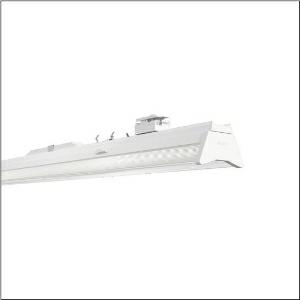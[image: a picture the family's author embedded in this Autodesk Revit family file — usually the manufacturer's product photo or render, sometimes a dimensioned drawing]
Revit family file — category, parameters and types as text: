
# Revit family: licross_r__11_performance_tw_51td16tnt85x_7c56
name_source: partatom
category: Lighting Fixtures
units: mm (PartAtom-declared; Revit-internal decimal feet)

## family parameters
Cut with Voids When Loaded = No
Host = Face
Light Source = No
Part Type = Normal
Room Calculation Point = No
Round Connector Dimension = Use Diameter
Shared = No

## types (1)
- --- (1 x LED 2700 K ... 6500 K, 8930 lm, 56 W, 2700K)
    Apparent Load = 56 VA
    CIE Flux Codes = 63 87 95 78 100
    Color Rendering = 80
    Color Temperature = 2700K
    Default Elevation = 1800 mm
    Description = Licross® 11 Performance TW, luminaire insert, of sheet steel, galvanised, coil coated, white, length: 1.500mm, width: 120mm, height: 123mm, LED rated luminous flux: 8.930lm, light colour: 8tw, control gear: DALI DT8, with plug, 5-pole, with phase selection, mains connection: 220..240V, AC, 50/60Hz, rated input power: 56W, internal wiring halogen-free, primary light control with lens, of plastic, primary optical cover: cover, of PMMA, light emission: direct/indirect distribution, primary light characteristic: symmetric, protection rating (complete): IP54, insulation class (complete): insulation class I (protective earthing), certification: CE, ENEC, VDE, UKCA, protection symbol: D if used in an environment with non-conductive dust loads with corresponding accessories, impact resistance: IK06, permissible ambient temperature for indoor applications: -25..+35°C, corresponds to IFS (International Featured Standards) requirements for safety and quality in the food industry, reducing of maximum allowable ambient temperature of 5°C with ceiling mounting, LABS conformity tested according to VDMA 24364:2018-05, packaging unit: 1 piece
    Height = 114 mm
    Lamp = 1 x LED 2700 K ... 6500 K
    Lamp Light Flux = 8930 lm
    Lamp Power = 56 W
    Lamp count = 1
    Length = 1500 mm
    Luminous efficacy = 159 lm/W
    Manufacturer = Siteco
    ModVariant = No
    Model = 51TD16TNT85X
    Mounting Place = Ceiling
    Mounting Type = Pendant
    Number of Poles = 1
    OnlyDefault = Yes
    Power Factor = 1
    Product Name = Licross® 11 Performance TW
    Product group = luminaire insert | ceiling pendant
    ProductGroupID = 902
    Protection Class = Protection class I
    Protection Degree = IP 54
    RLX_Detail_Level = 1
    RLX_Emergency_Light_Flux = 0 lm
    RLX_Emergency_Type = 0
    RLX_Emergency_Type_DB = No
    RlxData = <blob elided: 30401 chars, md5=60fe65d8>
    Socket = socket
    Standby Power = 0 W
    System Light Flux = 8930 lm
    System Power = 56 W
    Type Comments = individual setting: CCT=2700K
    Type Image = l_1256138.jpg
    URL = http://relux.com
    VarID = @adj_070089
    Voltage = 0 V
    Weight = 0.00 kg
    Width = 120 mm

## geometry (parser evidence)
native form markers: Blend x4, Sweep x9
no freeform markers — native parametric forms only
